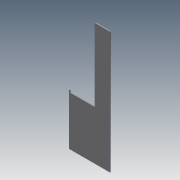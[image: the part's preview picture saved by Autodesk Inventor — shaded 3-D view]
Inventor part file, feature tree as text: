
AUTODESK INVENTOR PART (.ipt)
format: ipt  version: 2011 (Build 150239000, 239)  size: 161,280 bytes
history: native  units: in
note: dims shown in document units (in); Inventor stores cm internally (conversion verified against a paired STEP export)
features: extrude x12, sketch x12
ambient origin geometry x8: Origin, YZ Plane, XZ Plane, XY Plane, X Axis, Y Axis, Z Axis, Center Point
bodies: Solid1 (feature_tree)
feature tree (24):
  extrude  "Extrusion1"  Depth=35.0in
  extrude  "Extrusion2"  Depth=18.14in
  extrude  "Extrusion3"  Depth=0.25in TaperAngle=0.0deg
  extrude  "Extrusion4"  Depth=0.25in TaperAngle=0.0deg
  extrude  "Extrusion5"  Depth=0.25in TaperAngle=0.0deg
  extrude  "Extrusion6"  Depth=12.75in
  extrude  "Extrusion7"  Depth=0.5in
  extrude  "Extrusion8"  Depth=0.25in
  extrude  "Extrusion9"  Depth=0.25in TaperAngle=0.0deg
  extrude  "Extrusion10"  Depth=0.25in TaperAngle=0.0deg
  extrude  "Extrusion11"  Depth=0.185in
  extrude  "Extrusion12"  Depth=9.075in
  sketch  "Sketch1"  dims[d0=10.0in d1=35.0in]
  sketch  "Sketch2"  dims[d2=6.0in d3=18.14in]
  sketch  "Sketch3"  dims[d4=0.25in d5=0.0in d6=0.25in d7=0.0in]
  sketch  "Sketch4"  dims[d8=0.125in d9=0.25in d10=0.0in]
  sketch  "Sketch5"  dims[d11=0.25in d12=0.0in d13=0.25in d14=0.0in]
  sketch  "Sketch6"  dims[d15=0.25in d16=0.0in d17=12.75in]
  sketch  "Sketch7"  dims[d18=1.0in d19=0.0in d20=0.5in]
  sketch  "Sketch8"  dims[d21=1.0in d22=0.0in d23=0.25in]
  sketch  "Sketch9"  dims[d24=0.5in d25=0.25in d26=0.0in]
  sketch  "Sketch10"  dims[d27=0.75in d28=0.25in d29=0.0in]
  sketch  "Sketch11"  dims[d30=20.0in d31=0.185in]
  sketch  "Sketch12"  dims[d32=1.0in d33=0.0in d34=9.075in d35=1.0in d36=0.0in]
